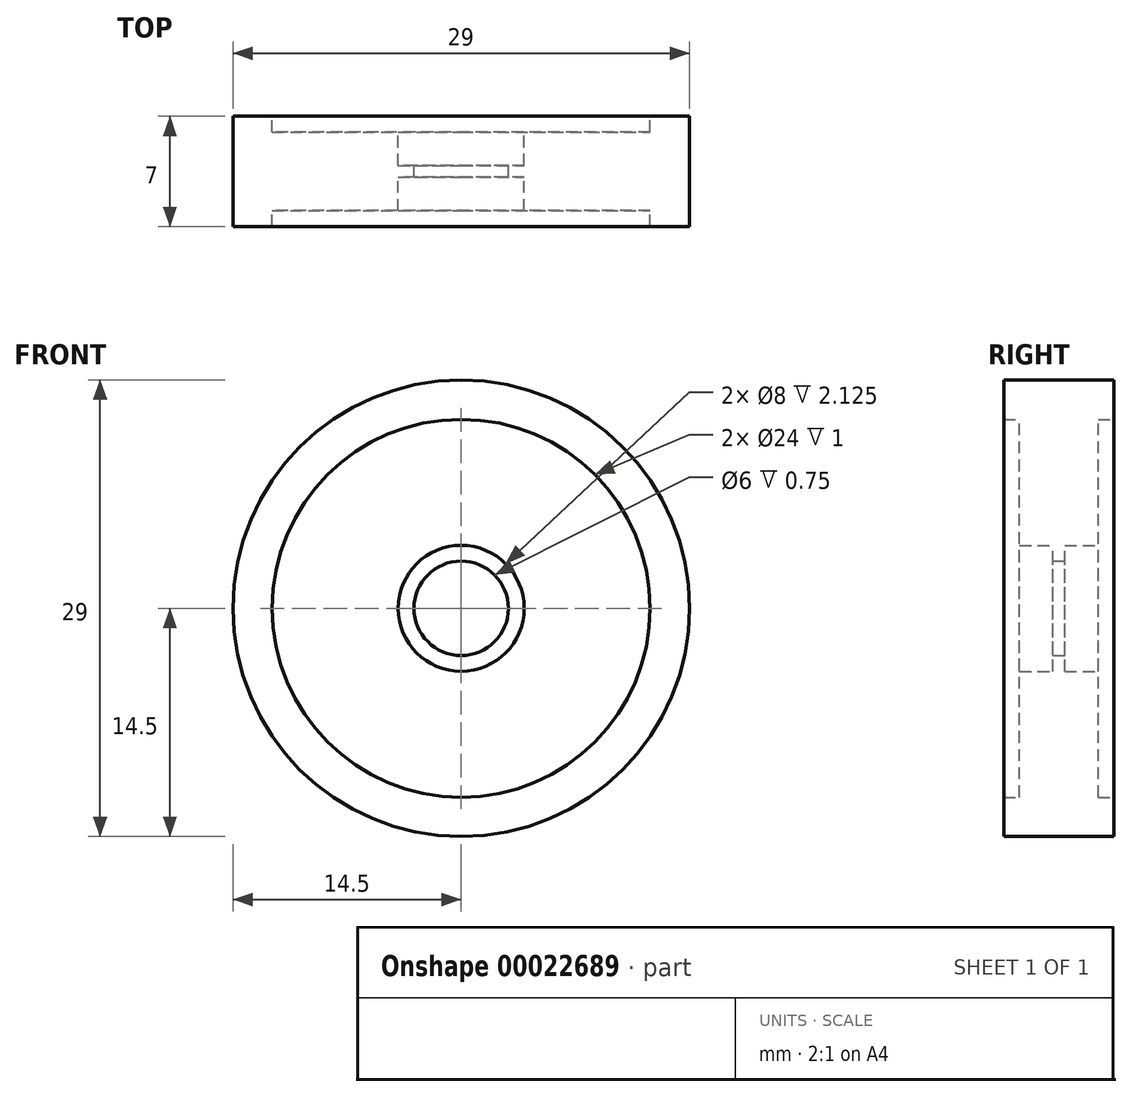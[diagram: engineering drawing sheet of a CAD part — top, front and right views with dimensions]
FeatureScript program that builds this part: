
annotation { "Feature Type Name" : "Feature", "Feature Type Description" : "" }
export const myFeature = defineFeature(function(context is Context, id is Id, definition is map)
    precondition{}
    {
        {
            var Q0;
            Q0=qCreatedBy(makeId("Front.planeOp"),FACE);
            var sketch = newSketch(context, id + "F0", { "sketchPlane" : qUnion([Q0])});
            skCircle(sketch, "E0", {"center": v(0, 0) * mm, "radius": 3 * mm});
            skCircle(sketch, "E1", {"center": v(0, 0) * mm, "radius": 12 * mm});
            skCircle(sketch, "E2", {"center": v(0, 0) * mm, "radius": 14.5 * mm});
            skCircle(sketch, "E3", {"center": v(0, 0) * mm, "radius": 4 * mm});
            skSolve(sketch);
        }
        {
            var Q0;
            Q0=makeQuery(id+"F0.imprint","IMPRINT",FACE,{"disambiguationData":[TD([[makeQuery(id+"F0.imprint","IMPRINT",EDGE,{"derivedFrom":sQuery(id+"F0.wireOp",EDGE,"E1")}),-1.0]])]});
            extrude(context, id + "F1", {"entities" : qUnion([Q0]), "endBound" : BoundingType.SYMMETRIC, "depth" : 7 * mm});
        }
        {
            var Q0;
            Q0=makeQuery(id+"F0.imprint","IMPRINT",FACE,{"disambiguationData":[TD([[makeQuery(id+"F0.imprint","IMPRINT",EDGE,{"derivedFrom":sQuery(id+"F0.wireOp",EDGE,"E1")}),1.0]])]});
            extrude(context, id + "F2", {"entities" : qUnion([Q0]), "operationType" : NewBodyOperationType.ADD, "endBound" : BoundingType.SYMMETRIC, "depth" : 5 * mm});
        }
        {
            var Q0;
            Q0=makeQuery(id+"F0.imprint","IMPRINT",FACE,{"disambiguationData":[TD([[makeQuery(id+"F0.imprint","IMPRINT",EDGE,{"derivedFrom":sQuery(id+"F0.wireOp",EDGE,"E0")}),-1.0]])]});
            extrude(context, id + "F3", {"entities" : qUnion([Q0]), "operationType" : NewBodyOperationType.ADD, "endBound" : BoundingType.SYMMETRIC, "depth" : .75 * mm});
        }
    });
